# Revit family: C_NPB255SO_2DO_Cad_MULT_Prod
name_source: partatom
category: Detail Items
revit_build: Autodesk Revit 2014 (Build: 20130308_1515(x64)
units: mm (PartAtom-declared; Revit-internal decimal feet)

## types (4) — shared parameters
Density = 1.73 kg
Description = Nail plate
EPD = https://www.strongtie.eu
ETA / DoP = https://www.strongtie.eu
Manufacturer = Simpson Strong-Tie
Model = NPB255SO
Model Disclaimer = Contact Simpson Strong-Tie Company  for more information
Model ID = 0292119625608525553367659087694597569061
Name = NPB255SO
ObjectType = NPB255SO
Product Material = Galvanised
Product Type = Nail plate
Reference = NPB255SO
Technical datasheet = https://www.strongtie.eu
URL = www.strongtie.eu
UniClass Number = Joist hangers
UniClass Title = Pr_20_29_31_44

## per-type parameters (varying)
| type | _visiblefront | _visibleleft | _visibleright | _visibletop |
| SST_NPB255SO_Front | Yes | No | No | No |
| SST_NPB255SO_Top | No | No | No | Yes |
| SST_NPB255SO_Left | No | Yes | No | No |
| SST_NPB255SO_Right | No | No | Yes | No |

## geometry (parser evidence)
native form markers: Sweep x1
no freeform markers — native parametric forms only
